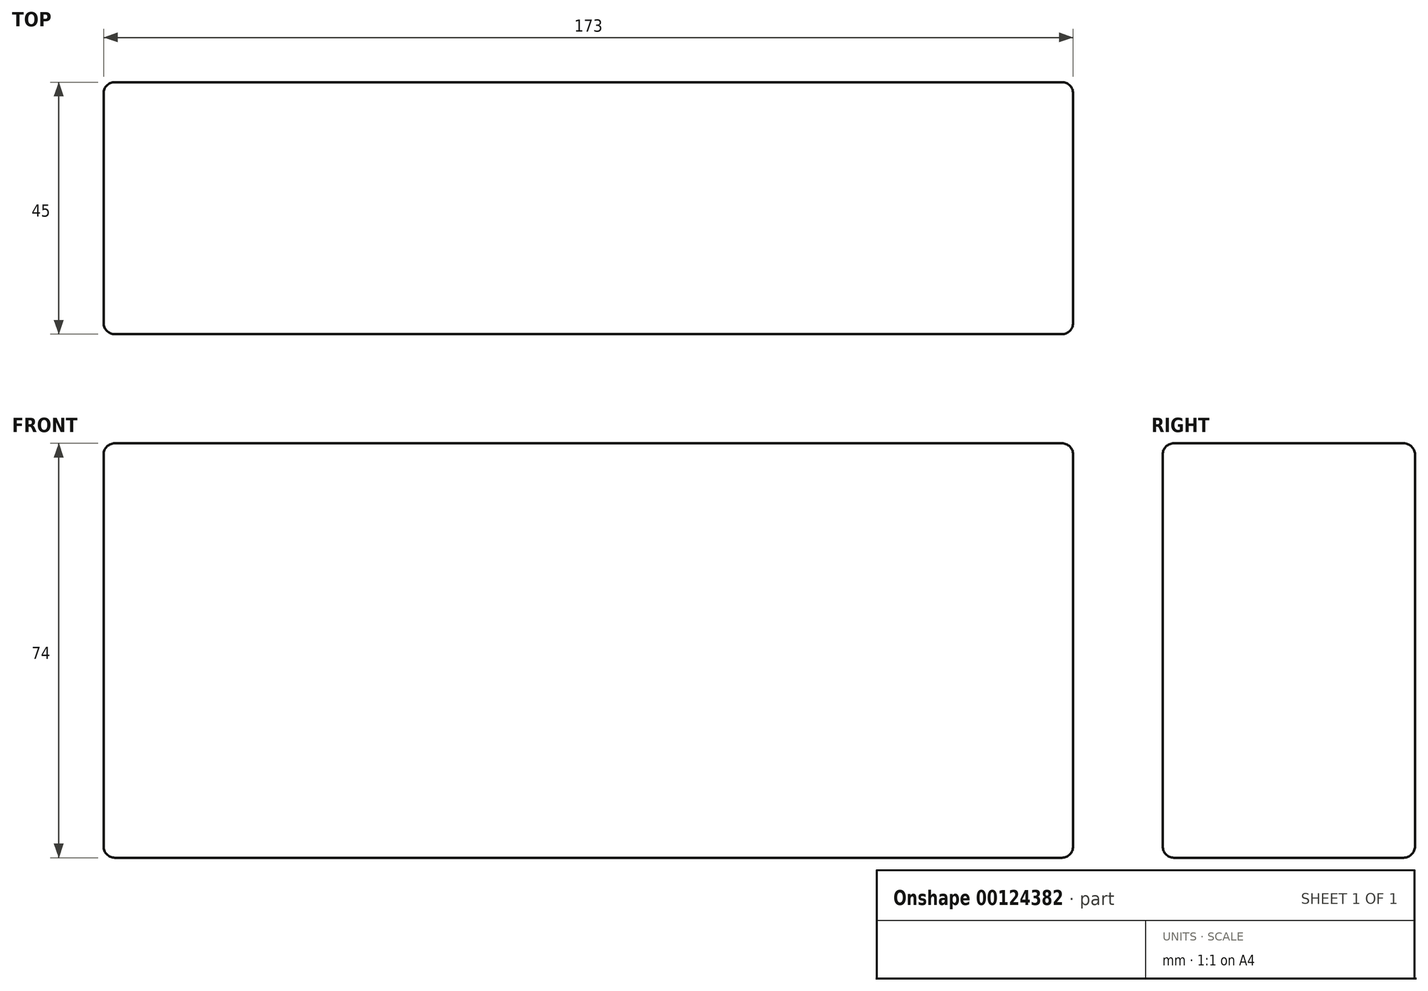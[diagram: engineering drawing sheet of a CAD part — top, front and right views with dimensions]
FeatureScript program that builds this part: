
annotation { "Feature Type Name" : "Feature", "Feature Type Description" : "" }
export const myFeature = defineFeature(function(context is Context, id is Id, definition is map)
    precondition{}
    {
        {
            var Q0;
            Q0=qCreatedBy(makeId("Front.planeOp"),FACE);
            var sketch = newSketch(context, id + "F0", { "sketchPlane" : qUnion([Q0])});
            skLineSegment(sketch, "E0.bottom", {"start": v(-81.12, 47.05) * mm, "end": v(91.88, 47.05) * mm});
            skLineSegment(sketch, "E0.top", {"start": v(-81.12, -26.95) * mm, "end": v(91.88, -26.95) * mm});
            skLineSegment(sketch, "E0.left", {"start": v(-81.12, 47.05) * mm, "end": v(-81.12, -26.95) * mm});
            skLineSegment(sketch, "E0.right", {"start": v(91.88, 47.05) * mm, "end": v(91.88, -26.95) * mm});
            skSolve(sketch);
        }
        {
            var Q0;
            Q0=makeQuery(id+"F0.imprint","IMPRINT",FACE,{"disambiguationData":[TD([[makeQuery(id+"F0.imprint","IMPRINT",EDGE,{"derivedFrom":sQuery(id+"F0.wireOp",EDGE,"E0.bottom")}),-1.0]])]});
            extrude(context, id + "F1", {"entities" : qUnion([Q0]), "depth" : 45 * mm});
        }
        {
            var Q0;
            Q0=makeQuery(id+"F1.opExtrude","CAP_EDGE",EDGE,{"disambiguationData":[OSD([sQuery(id+"F0.wireOp",EDGE,"E0.bottom")])],"isStart":false});
            var Q1;
            Q1=makeQuery(id+"F1.opExtrude","CAP_EDGE",EDGE,{"disambiguationData":[OSD([sQuery(id+"F0.wireOp",EDGE,"E0.bottom")])],"isStart":true});
            var Q2;
            Q2=makeQuery(id+"F1.opExtrude","CAP_EDGE",EDGE,{"disambiguationData":[OSD([sQuery(id+"F0.wireOp",EDGE,"E0.top")])],"isStart":false});
            var Q3;
            Q3=makeQuery(id+"F1.opExtrude","CAP_EDGE",EDGE,{"disambiguationData":[OSD([sQuery(id+"F0.wireOp",EDGE,"E0.top")])],"isStart":true});
            var Q4;
            Q4=makeQuery(id+"F1.opExtrude","CAP_FACE",FACE,{"disambiguationData":[OSD([sQuery(id+"F0.wireOp",EDGE,"E0.bottom"),sQuery(id+"F0.wireOp",EDGE,"E0.top"),sQuery(id+"F0.wireOp",EDGE,"E0.left"),sQuery(id+"F0.wireOp",EDGE,"E0.right")])],"isStart":false});
            var Q5;
            Q5=makeQuery(id+"F1.opExtrude","CAP_EDGE",EDGE,{"disambiguationData":[OSD([sQuery(id+"F0.wireOp",EDGE,"E0.right")])],"isStart":true});
            var Q6;
            Q6=makeQuery(id+"F1.opExtrude","SWEPT_FACE",FACE,{"disambiguationData":[OSD([sQuery(id+"F0.wireOp",EDGE,"E0.right")])]});
            var Q7;
            Q7=makeQuery(id+"F1.opExtrude","SWEPT_EDGE",EDGE,{"disambiguationData":[OSD([sQuery(id+"F0.wireOp",EDGE,"E0.bottom"),sQuery(id+"F0.wireOp",EDGE,"E0.left")])]});
            var Q8;
            Q8=makeQuery(id+"F1.opExtrude","CAP_EDGE",EDGE,{"disambiguationData":[OSD([sQuery(id+"F0.wireOp",EDGE,"E0.left")])],"isStart":true});
            var Q9;
            Q9=makeQuery(id+"F1.opExtrude","SWEPT_EDGE",EDGE,{"disambiguationData":[OSD([sQuery(id+"F0.wireOp",EDGE,"E0.top"),sQuery(id+"F0.wireOp",EDGE,"E0.left")])]});
            fillet(context, id + "F2", {"entities" : qUnion([Q0, Q1, Q2, Q3, Q4, Q5, Q6, Q7, Q8, Q9]), "radius" : 2 * mm, "tangentPropagation" : true, "allowEdgeOverflow" : false});
        }
    });
